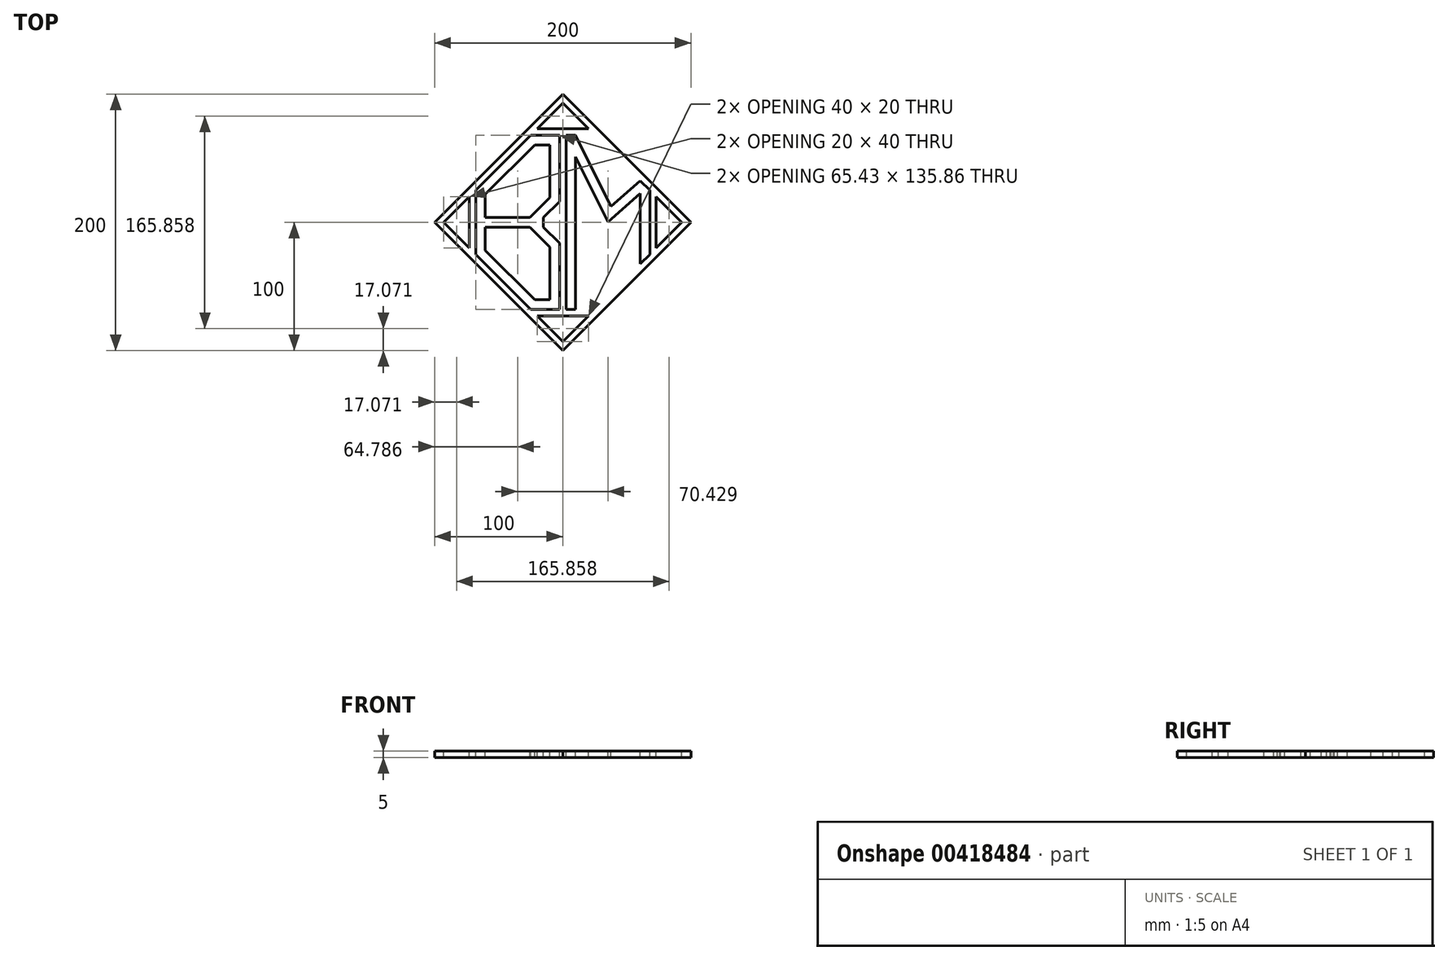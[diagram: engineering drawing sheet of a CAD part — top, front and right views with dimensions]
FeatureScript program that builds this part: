
annotation { "Feature Type Name" : "Feature", "Feature Type Description" : "" }
export const myFeature = defineFeature(function(context is Context, id is Id, definition is map)
    precondition{}
    {
        {
            var Q0;
            Q0=qCreatedBy(makeId("Top.planeOp"),FACE);
            var sketch = newSketch(context, id + "F0", { "sketchPlane" : qUnion([Q0])});
            skLineSegment(sketch, "E0", {"start": v(0, 100) * mm, "end": v(100, 0) * mm});
            skLineSegment(sketch, "E1", {"start": v(100, 0) * mm, "end": v(0, -100) * mm});
            skLineSegment(sketch, "E2", {"start": v(0, -100) * mm, "end": v(-100, 0) * mm});
            skLineSegment(sketch, "E3", {"start": v(-100, 0) * mm, "end": v(0, 100) * mm});
            skSolve(sketch);
        }
        {
            var Q0;
            Q0=makeQuery(id+"F0.imprint","IMPRINT",FACE,{"disambiguationData":[TD([[makeQuery(id+"F0.imprint","IMPRINT",EDGE,{"derivedFrom":sQuery(id+"F0.wireOp",EDGE,"E0")}),-1.0]])]});
            extrude(context, id + "F1", {"entities" : qUnion([Q0]), "depth" : 5 * mm});
        }
        {
            var Q0;
            Q0=makeQuery(id+"F1.opExtrude","CAP_FACE",FACE,{"disambiguationData":[OSD([sQuery(id+"F0.wireOp",EDGE,"E0"),sQuery(id+"F0.wireOp",EDGE,"E1"),sQuery(id+"F0.wireOp",EDGE,"E2"),sQuery(id+"F0.wireOp",EDGE,"E3")])],"isStart":false});
            var sketch = newSketch(context, id + "F2", { "sketchPlane" : qUnion([Q0])});
            skLineSegment(sketch, "E4", {"start": v(-72.93, -20) * mm, "end": v(-92.93, 0) * mm});
            skLineSegment(sketch, "E5", {"start": v(-92.93, 0) * mm, "end": v(-72.93, 20) * mm});
            skLineSegment(sketch, "E6", {"start": v(-72.93, 20) * mm, "end": v(-72.93, -20) * mm});
            skLineSegment(sketch, "E7.1.0", {"start": v(20, -72.93) * mm, "end": v(0, -92.93) * mm});
            skLineSegment(sketch, "E7.1.1", {"start": v(0, -92.93) * mm, "end": v(-20, -72.93) * mm});
            skLineSegment(sketch, "E7.1.2", {"start": v(-20, -72.93) * mm, "end": v(20, -72.93) * mm});
            skLineSegment(sketch, "E7.2.0", {"start": v(72.93, 20) * mm, "end": v(92.93, 0) * mm});
            skLineSegment(sketch, "E7.2.1", {"start": v(92.93, 0) * mm, "end": v(72.93, -20) * mm});
            skLineSegment(sketch, "E7.2.2", {"start": v(72.93, -20) * mm, "end": v(72.93, 20) * mm});
            skLineSegment(sketch, "E7.3.0", {"start": v(-20, 72.93) * mm, "end": v(0, 92.93) * mm});
            skLineSegment(sketch, "E7.3.1", {"start": v(0, 92.93) * mm, "end": v(20, 72.93) * mm});
            skLineSegment(sketch, "E7.3.2", {"start": v(20, 72.93) * mm, "end": v(-20, 72.93) * mm});
            skPoint(sketch, "E7.center", {"position": v(0, 0) * mm});
            skSolve(sketch);
        }
        {
            var Q0;
            Q0=makeQuery(id+"F2.imprint","IMPRINT",FACE,{"disambiguationData":[TD([[makeQuery(id+"F2.imprint","IMPRINT",EDGE,{"derivedFrom":sQuery(id+"F2.wireOp",EDGE,"E4")}),-1.0]])]});
            var Q1;
            Q1=makeQuery(id+"F2.imprint","IMPRINT",FACE,{"disambiguationData":[TD([[makeQuery(id+"F2.imprint","IMPRINT",EDGE,{"derivedFrom":sQuery(id+"F2.wireOp",EDGE,"E7.3.0")}),-1.0]])]});
            var Q2;
            Q2=makeQuery(id+"F2.imprint","IMPRINT",FACE,{"disambiguationData":[TD([[makeQuery(id+"F2.imprint","IMPRINT",EDGE,{"derivedFrom":sQuery(id+"F2.wireOp",EDGE,"E7.2.0")}),-1.0]])]});
            var Q3;
            Q3=makeQuery(id+"F2.imprint","IMPRINT",FACE,{"disambiguationData":[TD([[makeQuery(id+"F2.imprint","IMPRINT",EDGE,{"derivedFrom":sQuery(id+"F2.wireOp",EDGE,"E7.1.0")}),-1.0]])]});
            extrude(context, id + "F3", {"entities" : qUnion([Q0, Q1, Q2, Q3]), "operationType" : NewBodyOperationType.REMOVE, "endBound" : BoundingType.THROUGH_ALL, "oppositeDirection" : true, "depth" : 25 * mm});
        }
        {
            var Q0;
            Q0=makeQuery(id+"F1.opExtrude","CAP_FACE",FACE,{"disambiguationData":[OSD([sQuery(id+"F0.wireOp",EDGE,"E0"),sQuery(id+"F0.wireOp",EDGE,"E1"),sQuery(id+"F0.wireOp",EDGE,"E2"),sQuery(id+"F0.wireOp",EDGE,"E3")])],"isStart":false});
            var sketch = newSketch(context, id + "F4", { "sketchPlane" : qUnion([Q0])});
            skLineSegment(sketch, "E8", {"start": v(-67.93, -25) * mm, "end": v(-67.93, 25) * mm});
            skLineSegment(sketch, "E9", {"start": v(-67.93, 25) * mm, "end": v(-25, 67.93) * mm});
            skLineSegment(sketch, "E10", {"start": v(-67.93, -25) * mm, "end": v(-25, -67.93) * mm});
            skLineSegment(sketch, "E11", {"start": v(-25, -67.93) * mm, "end": v(-2.5, -67.93) * mm});
            skLineSegment(sketch, "E12", {"start": v(-25, 67.93) * mm, "end": v(-2.5, 67.93) * mm});
            skLineSegment(sketch, "E13", {"start": v(0, -72.93) * mm, "end": v(0, 72.93) * mm, "construction": true});
            skLineSegment(sketch, "E14", {"start": v(-2.5, 67.93) * mm, "end": v(-2.5, 16.25) * mm});
            skLineSegment(sketch, "E15", {"start": v(-2.5, 16.25) * mm, "end": v(-15, 3.75) * mm});
            skLineSegment(sketch, "E16", {"start": v(-15, -3.75) * mm, "end": v(-2.5, -16.25) * mm});
            skLineSegment(sketch, "E17", {"start": v(-2.5, -16.25) * mm, "end": v(-2.5, -67.93) * mm});
            skLineSegment(sketch, "E18", {"start": v(-60.43, -21.9) * mm, "end": v(-21.9, -60.43) * mm});
            skLineSegment(sketch, "E19", {"start": v(-21.9, -60.43) * mm, "end": v(-10, -60.43) * mm});
            skLineSegment(sketch, "E20", {"start": v(-10, -60.43) * mm, "end": v(-10, -19.36) * mm});
            skLineSegment(sketch, "E21", {"start": v(-10, -19.36) * mm, "end": v(-25.6, -3.75) * mm});
            skLineSegment(sketch, "E22", {"start": v(-25.6, -3.75) * mm, "end": v(-60.43, -3.75) * mm});
            skLineSegment(sketch, "E23", {"start": v(-60.43, -3.75) * mm, "end": v(-60.43, -21.9) * mm});
            skLineSegment(sketch, "E24", {"start": v(-15, -3.75) * mm, "end": v(-15, 3.75) * mm});
            skLineSegment(sketch, "E25", {"start": v(-21.9, 60.43) * mm, "end": v(-60.43, 21.9) * mm});
            skLineSegment(sketch, "E26", {"start": v(-60.43, 21.9) * mm, "end": v(-60.43, 3.75) * mm});
            skLineSegment(sketch, "E27", {"start": v(-60.43, 3.75) * mm, "end": v(-25.6, 3.75) * mm});
            skLineSegment(sketch, "E28", {"start": v(-25.6, 3.75) * mm, "end": v(-10, 19.36) * mm});
            skLineSegment(sketch, "E29", {"start": v(-10, 19.36) * mm, "end": v(-10, 60.43) * mm});
            skLineSegment(sketch, "E30", {"start": v(-10, 60.43) * mm, "end": v(-21.9, 60.43) * mm});
            skSolve(sketch);
        }
        {
            var Q0;
            {var subQ0=sQuery(id+"F0.wireOp",EDGE,"E2");var subQ1=sQuery(id+"F0.wireOp",EDGE,"E1");var subQ2=sQuery(id+"F0.wireOp",EDGE,"E3");var subQ3=sQuery(id+"F0.wireOp",EDGE,"E0");Q0=makeQuery(id+"F6.boolean.opBoolean","SPLIT",FACE,{"disambiguationData":[TD([makeQuery(id+"F1.opExtrude","SWEPT_FACE",FACE,{"disambiguationData":[OSD([subQ3])]})])],"derivedFrom":makeQuery(id+"F1.opExtrude","CAP_FACE",FACE,{"disambiguationData":[OSD([subQ3,subQ1,subQ0,subQ2])],"isStart":false})});}
            var sketch = newSketch(context, id + "F5", { "sketchPlane" : qUnion([Q0])});
            skLineSegment(sketch, "E31", {"start": v(2.5, -67.93) * mm, "end": v(2.5, 67.93) * mm});
            skLineSegment(sketch, "E32", {"start": v(2.5, 67.93) * mm, "end": v(10, 67.93) * mm});
            skLineSegment(sketch, "E33", {"start": v(10, 67.93) * mm, "end": v(37.58, 12.32) * mm});
            skLineSegment(sketch, "E34", {"start": v(37.58, 12.32) * mm, "end": v(60.43, 32.5) * mm});
            skLineSegment(sketch, "E35", {"start": v(60.43, 32.5) * mm, "end": v(67.93, 25) * mm});
            skLineSegment(sketch, "E36", {"start": v(67.93, 25) * mm, "end": v(67.93, -25) * mm});
            skLineSegment(sketch, "E37", {"start": v(67.93, -25) * mm, "end": v(60.43, -32.5) * mm});
            skLineSegment(sketch, "E38", {"start": v(60.43, -32.5) * mm, "end": v(60.43, 22.5) * mm});
            skLineSegment(sketch, "E39", {"start": v(60.43, 22.5) * mm, "end": v(35.21, 0.22) * mm});
            skLineSegment(sketch, "E40", {"start": v(35.21, 0.22) * mm, "end": v(10, 51.05) * mm});
            skLineSegment(sketch, "E41", {"start": v(10, 51.05) * mm, "end": v(10, -67.93) * mm});
            skLineSegment(sketch, "E42", {"start": v(10, -67.93) * mm, "end": v(2.5, -67.93) * mm});
            skLineSegment(sketch, "E43", {"start": v(0, -72.93) * mm, "end": v(0, 72.93) * mm, "construction": true});
            skLineSegment(sketch, "E44", {"start": v(10, -8.44) * mm, "end": v(60.43, -8.44) * mm, "construction": true});
            skLineSegment(sketch, "E45", {"start": v(35.21, 0.22) * mm, "end": v(35.21, -8.44) * mm, "construction": true});
            skSolve(sketch);
        }
        {
            var Q0;
            Q0 = qSketchRegion(id + "F5", true);
            var Q1;
            Q1 = qSketchRegion(id + "F4", true);
            extrude(context, id + "F6", {"entities" : qUnion([Q0, Q1]), "operationType" : NewBodyOperationType.REMOVE, "endBound" : BoundingType.THROUGH_ALL, "oppositeDirection" : true, "depth" : 25 * mm});
        }
    });
